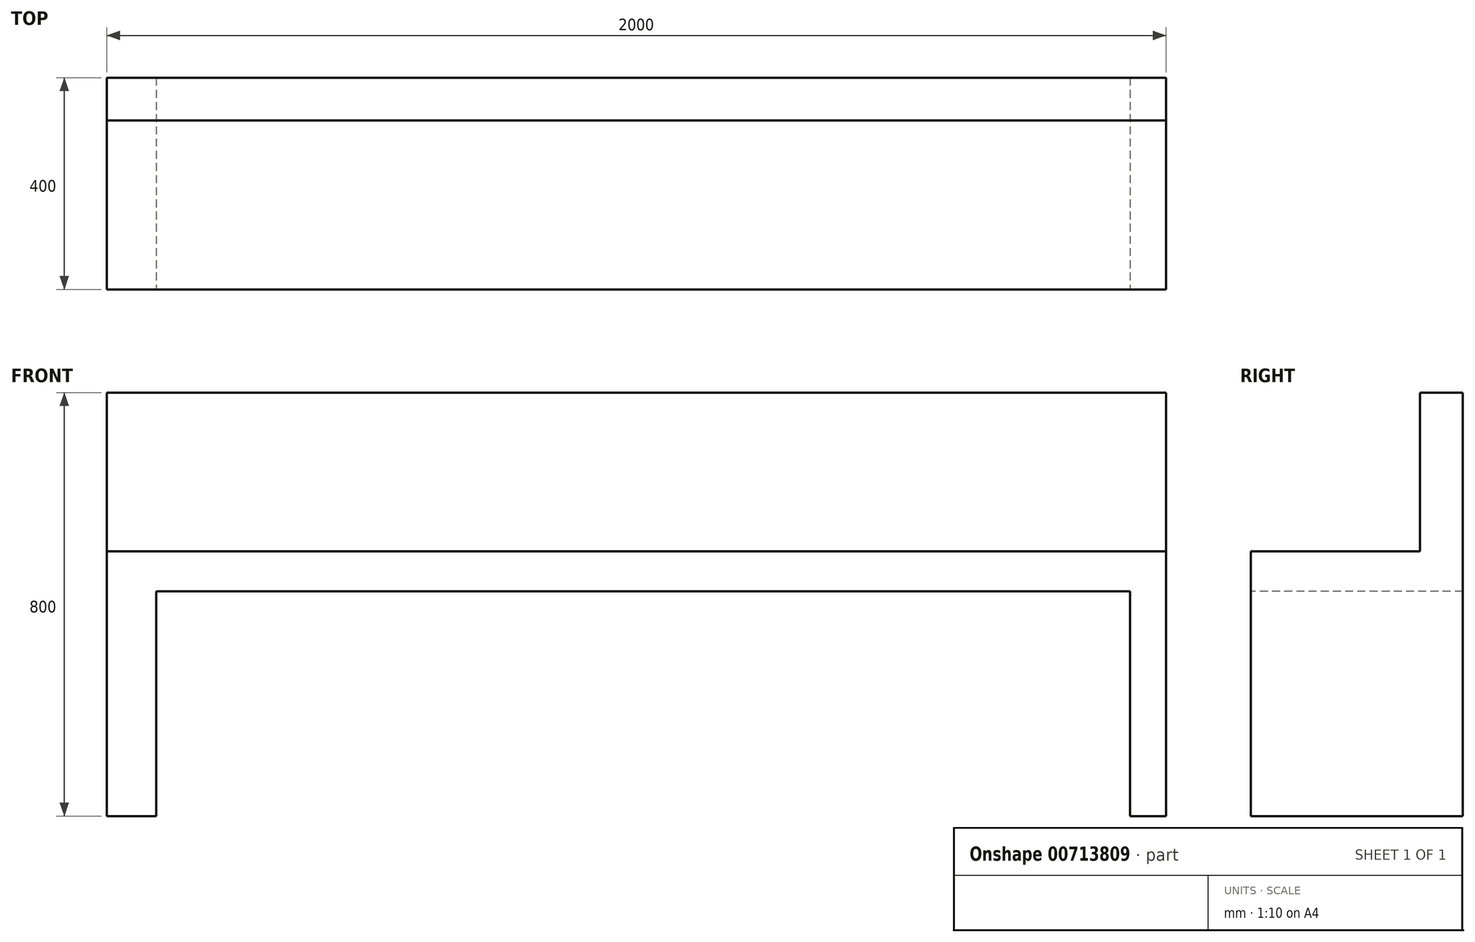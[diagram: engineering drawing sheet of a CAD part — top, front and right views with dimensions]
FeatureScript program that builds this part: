
annotation { "Feature Type Name" : "Feature", "Feature Type Description" : "" }
export const myFeature = defineFeature(function(context is Context, id is Id, definition is map)
    precondition{}
    {
        {
            var Q0;
            Q0=qCreatedBy(makeId("Front.planeOp"),FACE);
            var sketch = newSketch(context, id + "F0", { "sketchPlane" : qUnion([Q0])});
            skLineSegment(sketch, "E0.bottom", {"start": v(0, 0) * mm, "end": v(2000, 0) * mm});
            skLineSegment(sketch, "E0.top", {"start": v(0, 500) * mm, "end": v(2000, 500) * mm});
            skLineSegment(sketch, "E0.left", {"start": v(0, 0) * mm, "end": v(0, 500) * mm});
            skLineSegment(sketch, "E0.right", {"start": v(2000, 0) * mm, "end": v(2000, 500) * mm});
            skSolve(sketch);
        }
        {
            var Q0;
            Q0=makeQuery(id+"F0.imprint","IMPRINT",FACE,{"disambiguationData":[TD([[makeQuery(id+"F0.imprint","IMPRINT",EDGE,{"derivedFrom":sQuery(id+"F0.wireOp",EDGE,"E0.bottom")}),1.0]])]});
            extrude(context, id + "F1", {"entities" : qUnion([Q0]), "depth" : 400 * mm, "offsetDistance" : 25 * mm});
        }
        {
            var Q0;
            Q0=makeQuery(id+"F1.opExtrude","CAP_FACE",FACE,{"disambiguationData":[OSD([sQuery(id+"F0.wireOp",EDGE,"E0.bottom"),sQuery(id+"F0.wireOp",EDGE,"E0.top"),sQuery(id+"F0.wireOp",EDGE,"E0.left"),sQuery(id+"F0.wireOp",EDGE,"E0.right")])],"isStart":false});
            var sketch = newSketch(context, id + "F2", { "sketchPlane" : qUnion([Q0])});
            skLineSegment(sketch, "E1.bottom", {"start": v(93.56, 0) * mm, "end": v(1932.04, 0) * mm});
            skLineSegment(sketch, "E1.top", {"start": v(93.56, 424.32) * mm, "end": v(1932.04, 424.32) * mm});
            skLineSegment(sketch, "E1.left", {"start": v(93.56, 0) * mm, "end": v(93.56, 424.32) * mm});
            skLineSegment(sketch, "E1.right", {"start": v(1932.04, 0) * mm, "end": v(1932.04, 424.32) * mm});
            skSolve(sketch);
        }
        {
            var Q0;
            Q0=makeQuery(id+"F2.imprint","IMPRINT",FACE,{"disambiguationData":[TD([[makeQuery(id+"F2.imprint","IMPRINT",EDGE,{"derivedFrom":sQuery(id+"F2.wireOp",EDGE,"E1.bottom")}),1.0]])]});
            extrude(context, id + "F3", {"entities" : qUnion([Q0]), "operationType" : NewBodyOperationType.REMOVE, "endBound" : BoundingType.UP_TO_NEXT, "oppositeDirection" : true, "depth" : 25 * mm, "offsetDistance" : 25 * mm});
        }
        {
            var Q0;
            Q0=makeQuery(id+"F1.opExtrude","SWEPT_FACE",FACE,{"disambiguationData":[OSD([sQuery(id+"F0.wireOp",EDGE,"E0.top")])]});
            var sketch = newSketch(context, id + "F4", { "sketchPlane" : qUnion([Q0])});
            skLineSegment(sketch, "E2.bottom", {"start": v(2000, 0) * mm, "end": v(0, 0) * mm});
            skLineSegment(sketch, "E2.top", {"start": v(2000, -80.58) * mm, "end": v(0, -80.58) * mm});
            skLineSegment(sketch, "E2.left", {"start": v(2000, 0) * mm, "end": v(2000, -80.58) * mm});
            skLineSegment(sketch, "E2.right", {"start": v(0, 0) * mm, "end": v(0, -80.58) * mm});
            skSolve(sketch);
        }
        {
            var Q0;
            Q0 = qSketchRegion(id + "F4", true);
            var Q1;
            Q1=makeQuery(id+"F4.imprint","IMPRINT",FACE,{"disambiguationData":[TD([[makeQuery(id+"F4.imprint","IMPRINT",EDGE,{"derivedFrom":sQuery(id+"F4.wireOp",EDGE,"E2.bottom")}),-1.0]])]});
            extrude(context, id + "F5", {"entities" : qUnion([Q0, Q1]), "operationType" : NewBodyOperationType.ADD, "depth" : 300 * mm, "offsetDistance" : 25 * mm});
        }
    });
